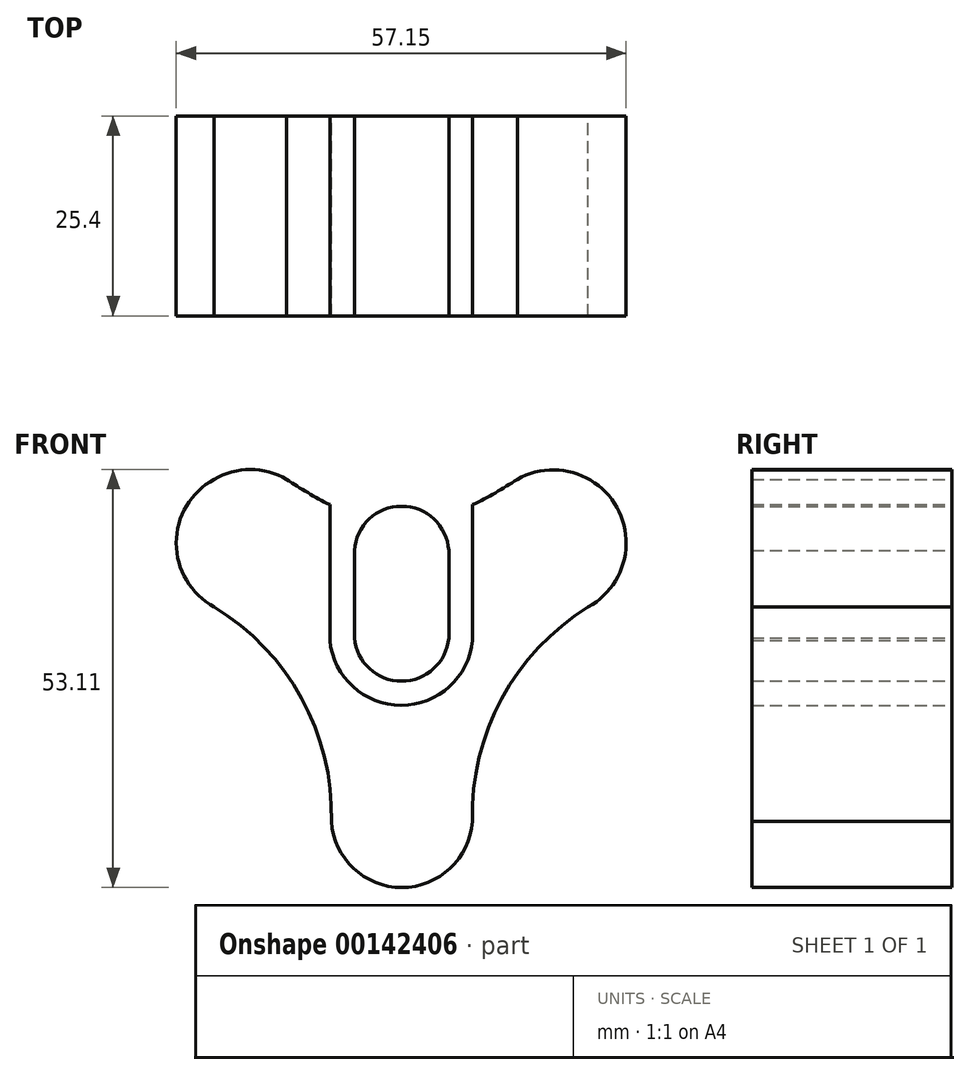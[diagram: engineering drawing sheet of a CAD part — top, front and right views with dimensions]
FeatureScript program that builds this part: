
annotation { "Feature Type Name" : "Feature", "Feature Type Description" : "" }
export const myFeature = defineFeature(function(context is Context, id is Id, definition is map)
    precondition{}
    {
        {
            var Q0;
            Q0=qCreatedBy(makeId("Front.planeOp"),FACE);
            var sketch = newSketch(context, id + "F0", { "sketchPlane" : qUnion([Q0])});
            skLineSegment(sketch, "E0", {"start": v(-8.95, 48.7) * mm, "end": v(-8.95, 31.48) * mm});
            skArc(sketch, "E1", {"start": v(-8.95, 31.48) * mm, "mid": v(0.11, 23.23) * mm, "end": v(9.18, 31.48) * mm});
            skLineSegment(sketch, "E2", {"start": v(-5.84, 42.87) * mm, "end": v(-5.84, 31.8) * mm});
            skLineSegment(sketch, "E3", {"start": v(6.15, 42.87) * mm, "end": v(6.15, 31.8) * mm});
            skArc(sketch, "E4", {"start": v(6.15, 42.87) * mm, "mid": v(0.16, 48.52) * mm, "end": v(-5.84, 42.87) * mm});
            skArc(sketch, "E5", {"start": v(-5.84, 31.8) * mm, "mid": v(0.16, 26.3) * mm, "end": v(6.15, 31.8) * mm});
            skPoint(sketch, "E6.endSnap0", {"position": v(0.16, 48.52) * mm});
            skLineSegment(sketch, "E7", {"start": v(9.18, 31.48) * mm, "end": v(9.18, 48.7) * mm});
            skArc(sketch, "E8", {"start": v(9.18, 48.7) * mm, "mid": v(12.08, 50.22) * mm, "end": v(14.86, 51.94) * mm});
            skArc(sketch, "E9", {"start": v(23.84, 35.72) * mm, "mid": v(27.52, 48.36) * mm, "end": v(14.86, 51.94) * mm});
            skArc(sketch, "E10", {"start": v(23.84, 35.72) * mm, "mid": v(12.88, 24.06) * mm, "end": v(9.14, 8.5) * mm});
            skArc(sketch, "E11", {"start": v(-8.75, 8.5) * mm, "mid": v(0.2, 0.08) * mm, "end": v(9.14, 8.5) * mm});
            skArc(sketch, "E12", {"start": v(-8.75, 8.5) * mm, "mid": v(-12.54, 24.11) * mm, "end": v(-23.66, 35.72) * mm});
            skArc(sketch, "E13", {"start": v(-23.66, 51.94) * mm, "mid": v(-28.47, 43.83) * mm, "end": v(-23.66, 35.72) * mm});
            skArc(sketch, "E14", {"start": v(-14.44, 51.94) * mm, "mid": v(-19.05, 53.19) * mm, "end": v(-23.66, 51.94) * mm});
            skArc(sketch, "E15", {"start": v(-14.44, 51.94) * mm, "mid": v(-11.75, 50.23) * mm, "end": v(-8.95, 48.7) * mm});
            skSolve(sketch);
        }
        {
            var Q0;
            Q0=makeQuery(id+"F0.imprint","IMPRINT",FACE,{"disambiguationData":[TD([[makeQuery(id+"F0.imprint","IMPRINT",EDGE,{"derivedFrom":sQuery(id+"F0.wireOp",EDGE,"E0")}),-1.0]])]});
            var Q1;
            Q1=makeQuery(id+"F0.imprint","IMPRINT",FACE,{"disambiguationData":[TD([[makeQuery(id+"F0.imprint","IMPRINT",EDGE,{"derivedFrom":sQuery(id+"F0.wireOp",EDGE,"E2")}),1.0]])]});
            extrude(context, id + "F1", {"entities" : qUnion([Q0, Q1]), "depth" : 25.4 * mm});
        }
    });
